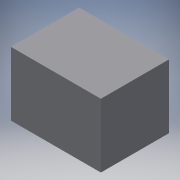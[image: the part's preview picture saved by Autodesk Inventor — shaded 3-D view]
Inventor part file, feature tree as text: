
AUTODESK INVENTOR PART (.ipt)
format: ipt  version: 2016 (Build 200138000, 138)  size: 93,184 bytes
history: native  units: mm
features: extrude x1, sketch x1
ambient origin geometry x8: Origin, YZ Plane, XZ Plane, XY Plane, X Axis, Y Axis, Z Axis, Center Point
bodies: Solid1 (feature_tree)
feature tree (2):
  extrude  "Extrusion1"  [1 undecoded]
  sketch  "Sketch1"  dims[d4=0.0mm]
note: 1 required parameter value undecoded (feature->parameter linkage not recoverable at this tier; creation-order binding heuristic only, values carry confidence <= 0.55)
